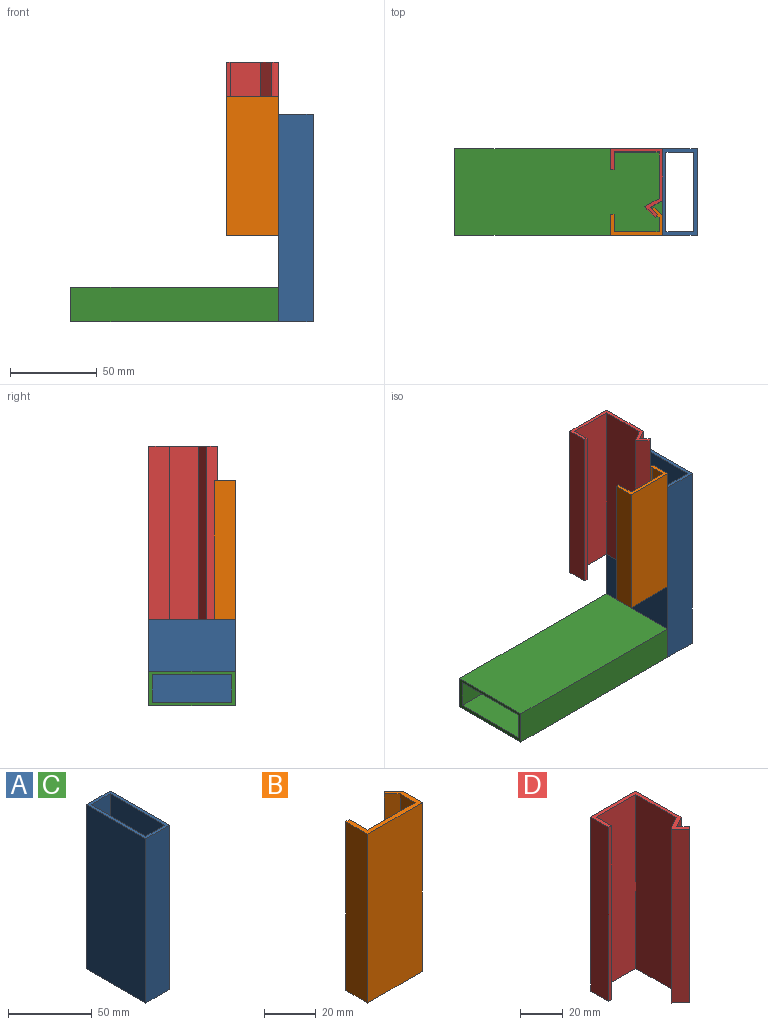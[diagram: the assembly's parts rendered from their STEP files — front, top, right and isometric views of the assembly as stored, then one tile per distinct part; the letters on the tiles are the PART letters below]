
ASSEMBLY  parts=4 mates=3
PART A: 10 faces, bbox 20x50x120 mm
  f0: plane 50x20mm, normal (0,0,1), area 264mm2, adj f2,f3,f4,f5,f6,f7,f8,f9
  f1: plane 50x20mm, normal (0,0,-1), area 264mm2, adj f2,f3,f4,f5,f6,f7,f8,f9
  f2: plane 120x16mm, normal (0,1,0), area 1920mm2, adj f0,f1,f3,f5
  f3: plane 120x46mm, normal (-1,0,0), area 5520mm2, adj f0,f1,f2,f4
  f4: plane 120x16mm, normal (0,-1,0), area 1920mm2, adj f0,f1,f3,f5
  f5: plane 120x46mm, normal (1,0,0), area 5520mm2, adj f0,f1,f2,f4
  f6: plane 120x20mm, normal (0,-1,0), area 2400mm2, adj f0,f1,f7,f9
  f7: plane 120x50mm, normal (1,0,0), area 6000mm2, adj f0,f1,f6,f8
  f8: plane 120x20mm, normal (0,1,0), area 2400mm2, adj f0,f1,f7,f9
  f9: plane 120x50mm, normal (-1,0,0), area 6000mm2, adj f0,f1,f6,f8
PART B: 12 faces, bbox 30x15.9x80 mm
  f0: plane 30x15.95mm, normal (0,0,-1), area 110.3mm2, adj f1,f3,f4,f5,f6,f7,f8,f9
  f1: plane 80x2mm, normal (0,1,0), area 160mm2, adj f0,f2,f7,f11
  f2: plane 30x15.95mm, normal (0,0,1), area 110.3mm2, adj f1,f3,f4,f5,f6,f7,f8,f9
  f3: plane 80x1.41mm, normal (-0.71,0.71,0), area 160mm2, adj f0,f2,f4,f8
  f4: plane 80x4.36mm, normal (-0.71,-0.71,0), area 493.7mm2, adj f0,f2,f3,f5
  f5: plane 80x8.17mm, normal (-1,0,0), area 653.7mm2, adj f0,f2,f4,f6
  f6: plane 80x26mm, normal (0,1,0), area 2080mm2, adj f0,f2,f5,f7
  f7: plane 80x10mm, normal (1,0,0), area 800mm2, adj f0,f1,f2,f6
  f8: plane 80x4.95mm, normal (0.71,0.71,0), area 560mm2, adj f0,f2,f3,f9
  f9: plane 80x11mm, normal (1,0,0), area 880mm2, adj f0,f2,f8,f10
  f10: plane 80x30mm, normal (0,-1,0), area 2400mm2, adj f0,f2,f9,f11
  f11: plane 80x12mm, normal (-1,0,0), area 960mm2, adj f0,f1,f2,f10
PART C: same geometry as A
PART D: 14 faces, bbox 30x39.7x100 mm
  f0: plane 39.66x30mm, normal (0,0,-1), area 166.9mm2, adj f1,f3,f4,f5,f6,f7,f8,f9
  f1: plane 100x1.41mm, normal (0.71,-0.71,0), area 200mm2, adj f0,f2,f8,f13
  f2: plane 39.66x30mm, normal (0,0,1), area 166.9mm2, adj f1,f3,f4,f5,f6,f7,f8,f9
  f3: plane 100x2mm, normal (0,-1,0), area 200mm2, adj f0,f2,f4,f9
  f4: plane 100x10mm, normal (1,0,0), area 1000mm2, adj f0,f2,f3,f5
  f5: plane 100x26mm, normal (0,-1,0), area 2600mm2, adj f0,f2,f4,f6
  f6: plane 100x26.85mm, normal (-1,0,0), area 2684.5mm2, adj f0,f2,f5,f7
  f7: plane 100x8.19mm, normal (-0.5,0.87,0), area 945.2mm2, adj f0,f2,f6,f8
  f8: plane 100x6.09mm, normal (-0.71,-0.71,0), area 860.6mm2, adj f0,f1,f2,f7
  f9: plane 100x12mm, normal (-1,0,0), area 1200mm2, adj f0,f2,f3,f10
  f10: plane 100x30mm, normal (0,1,0), area 3000mm2, adj f0,f2,f9,f11
  f11: plane 100x30mm, normal (1,0,0), area 3000mm2, adj f0,f2,f10,f12
  f12: plane 100x6.93mm, normal (0.5,-0.87,0), area 800mm2, adj f0,f2,f11,f13
  f13: plane 100x4.24mm, normal (0.71,0.71,0), area 600mm2, adj f0,f1,f2,f12
PLACE A t=(23.71,50.12,66.26)mm fixed
PLACE B t=(23.71,50.12,116.26)mm
PLACE C rot(axis=(0,1,0),90deg) t=(-66.29,50.12,116.26)mm
PLACE D t=(23.71,50.12,116.26)mm
MATE fastened A.f1 <-> C.f7  axis (0,0,-1) through (53.71,37.12,66.26)mm
MATE slider B.f10 <-> A.f6  axis (0,-1,0) through (53.71,12.12,116.26)mm
MATE slider D.f10 <-> A.f8  axis (0,1,0) through (53.71,62.12,116.26)mm
